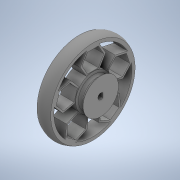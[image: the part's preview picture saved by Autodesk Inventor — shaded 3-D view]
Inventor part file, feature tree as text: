
AUTODESK INVENTOR PART (.ipt)
format: ipt  version: 2020 (Build 240168000, 168)  size: 411,648 bytes
history: native  units: in
note: dims shown in document units (in); Inventor stores cm internally (conversion verified against a paired STEP export)
features: sketch x4, extrude x2, revolve x2, projected_geometry x1
ambient origin geometry x8: Origin, YZ Plane, XZ Plane, XY Plane, X Axis, Y Axis, Z Axis, Center Point
bodies: Solid1 (feature_tree)
feature tree (9):
  extrude  "Extrusion1"  Depth=0.0394in
  sketch  "Sketch3"  dims[d6=0.7087in d7=0.1575in]
  revolve  "Revolution1"  [1 undecoded]
  extrude  "Extrusion2"  Depth=0.1575in
  revolve  "Revolution2"  [1 undecoded]
  sketch  "Sketch1"  dims[d0=0.1181in d1=0.0394in]
  sketch  "Sketch2"  dims[d3=1.6929in d4=0.1181in]
  projected_geometry  "Projected Loop1"
  sketch  "Sketch4"  dims[d8=0.0in d9=1.6929in d10=0.063in d11=0.0315in d16=0.2756in d17=0.0in d19=360.0deg d20=0.0787in d24=0.0394in d25=90.0deg d26=45.0deg d28=0.0079in d29=1.9685in d31=360.0deg]
note: 2 required parameter values undecoded (feature->parameter linkage not recoverable at this tier; creation-order binding heuristic only, values carry confidence <= 0.55)
